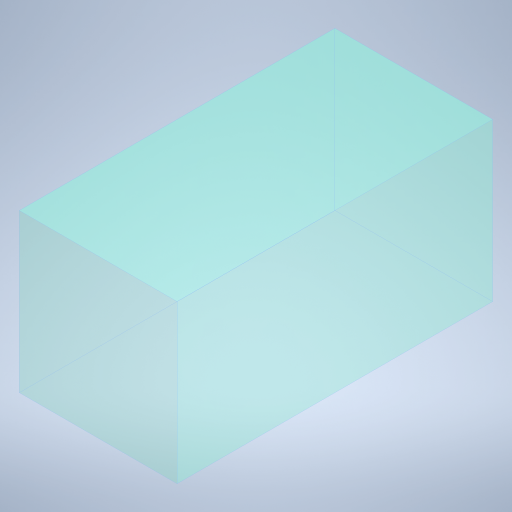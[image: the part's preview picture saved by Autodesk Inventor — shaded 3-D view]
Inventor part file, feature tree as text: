
AUTODESK INVENTOR PART (.ipt)
format: ipt  version: 2024 (Build 280153000, 153)  size: 230,912 bytes
history: native  units: in
note: dims shown in document units (in); Inventor stores cm internally (conversion verified against a paired STEP export)
features: extrude x1, sketch x1
ambient origin geometry x8: Origin, YZ Plane, XZ Plane, XY Plane, X Axis, Y Axis, Z Axis, Center Point
bodies: Solid1 (feature_tree)
feature tree (2):
  extrude  "Extrusion1"  Depth=36.0in
  sketch  "Sketch1"  dims[d0=36.0in d1=36.0in d2=72.0in d3=0.0in]
